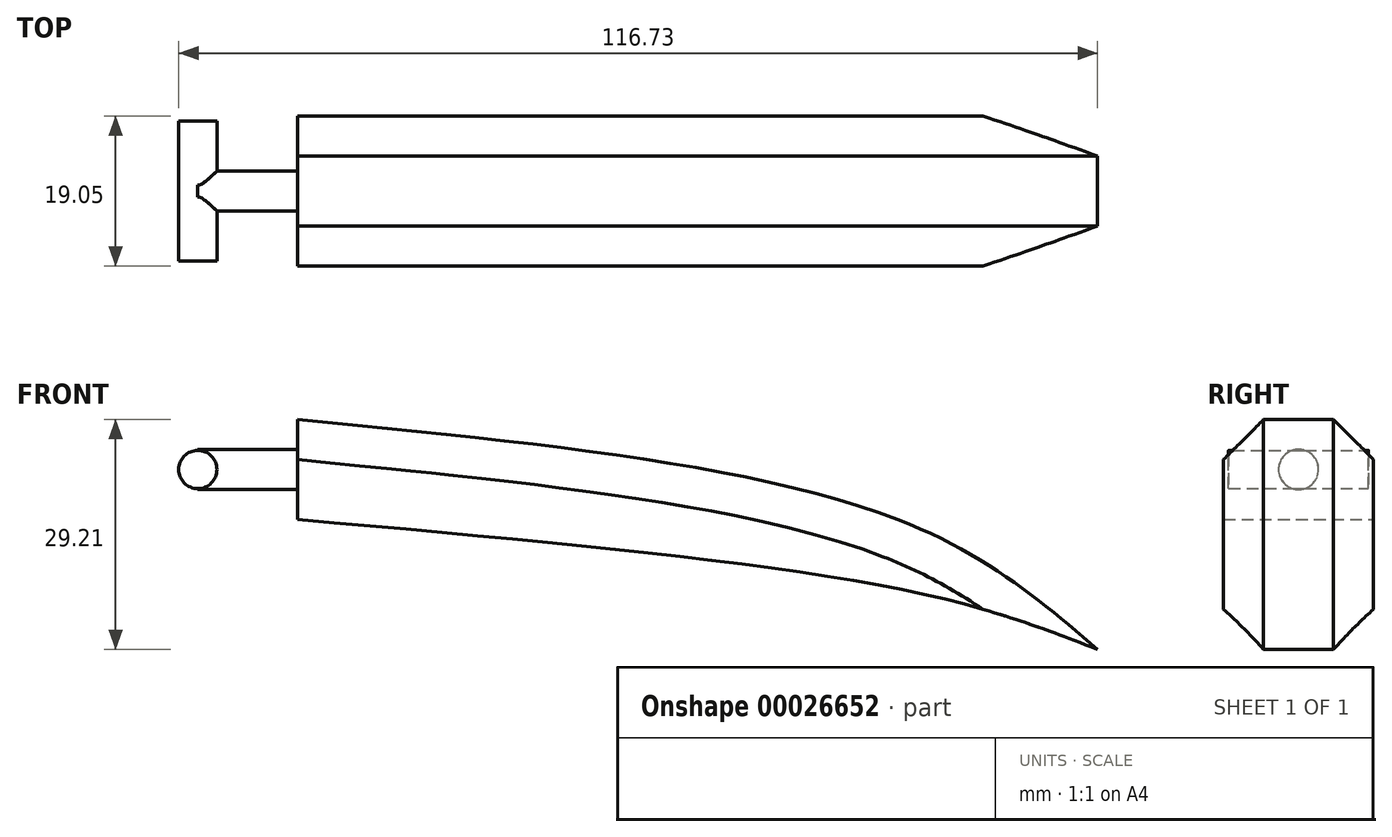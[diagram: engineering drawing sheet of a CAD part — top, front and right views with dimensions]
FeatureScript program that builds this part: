
annotation { "Feature Type Name" : "Feature", "Feature Type Description" : "" }
export const myFeature = defineFeature(function(context is Context, id is Id, definition is map)
    precondition{}
    {
        {
            var Q0;
            Q0=qCreatedBy(makeId("Front.planeOp"),FACE);
            var sketch = newSketch(context, id + "F0", { "sketchPlane" : qUnion([Q0])});
            skLineSegment(sketch, "E0.left", {"start": v(-50.09, 28.12) * mm, "end": v(-50.09, 40.82) * mm});
            skFitSpline(sketch, "E1", {"points": [v(-31.04, 40.82) * mm, v(26.11, 28.12) * mm, v(51.51, 11.61) * mm], "startDerivative": vector(109.54, -8.36) * mm, "endDerivative": vector(52.52, -44.36) * mm});
            skFitSpline(sketch, "E2", {"points": [v(-50.09, 28.12) * mm, v(28.13, 18.9) * mm, v(51.51, 11.61) * mm], "startDerivative": vector(139.98, -12.41) * mm, "endDerivative": vector(55.2, -21.46) * mm});
            skPoint(sketch, "E3.right.start.orphan", {"position": v(51.51, 31.93) * mm});
            skPoint(sketch, "E4.orphan", {"position": v(51.51, 40.82) * mm});
            skPoint(sketch, "E5.orphan", {"position": v(26.11, 40.82) * mm});
            skFitSpline(sketch, "E6", {"points": [v(-50.09, 40.82) * mm, v(26.11, 28.12) * mm, v(51.51, 11.61) * mm], "startDerivative": vector(141.74, -13.82) * mm, "endDerivative": vector(54.8, -47.15) * mm});
            skLineSegment(sketch, "E7.trimOffspring", {"start": v(51.51, 11.61) * mm, "end": v(51.51, 11.61) * mm});
            skSolve(sketch);
        }
        {
            var Q0;
            Q0 = qSketchRegion(id + "F0", true);
            extrude(context, id + "F1", {"entities" : qUnion([Q0]), "depth" : 19.05 * mm});
        }
        {
            var Q0;
            Q0=makeQuery(id+"F1.opExtrude","CAP_EDGE",EDGE,{"disambiguationData":[OSD([sQuery(id+"F0.wireOp",EDGE,"E6")])],"isStart":false});
            var Q1;
            Q1=makeQuery(id+"F1.opExtrude","CAP_EDGE",EDGE,{"disambiguationData":[OSD([sQuery(id+"F0.wireOp",EDGE,"E6")])],"isStart":true});
            var Q2;
            Q2=makeQuery(id+"F1.opExtrude","CAP_EDGE",EDGE,{"disambiguationData":[OSD([sQuery(id+"F0.wireOp",EDGE,"E1")])],"isStart":false});
            var Q3;
            Q3=makeQuery(id+"F1.opExtrude","CAP_EDGE",EDGE,{"disambiguationData":[OSD([sQuery(id+"F0.wireOp",EDGE,"E1")])],"isStart":true});
            chamfer(context, id + "F2", {"entities" : qUnion([Q0, Q1, Q2, Q3]), "width" : 5.08 * mm, "tangentPropagation" : true});
        }
        {
            var Q0;
            Q0=makeQuery(id+"F1.opExtrude","SWEPT_FACE",FACE,{"disambiguationData":[OSD([sQuery(id+"F0.wireOp",EDGE,"E0.left")])]});
            var sketch = newSketch(context, id + "F3", { "sketchPlane" : qUnion([Q0])});
            skCircle(sketch, "E8", {"center": v(9.53, 34.47) * mm, "radius": 2.54 * mm});
            skLineSegment(sketch, "E9", {"start": v(9.53, 28.12) * mm, "end": v(9.53, 40.82) * mm});
            skPoint(sketch, "E10", {"position": v(0, 35.72) * mm});
            skPoint(sketch, "E11", {"position": v(0, 28.12) * mm});
            skLineSegment(sketch, "E12", {"start": v(0, 35.72) * mm, "end": v(0, 28.12) * mm});
            skSolve(sketch);
        }
        {
            var Q0;
            Q0 = qSketchRegion(id + "F3", true);
            extrude(context, id + "F4", {"entities" : qUnion([Q0]), "operationType" : NewBodyOperationType.ADD, "depth" : 12.7 * mm});
        }
        {
            var Q0;
            Q0=makeQuery(id+"F4.opExtrude","CAP_FACE",FACE,{"disambiguationData":[OSD([sQuery(id+"F3.wireOp",EDGE,"E8")])],"isStart":false});
            var sketch = newSketch(context, id + "F5", { "sketchPlane" : qUnion([Q0])});
            skLineSegment(sketch, "E13.rect.bottom", {"start": v(0.64, 36.9) * mm, "end": v(18.42, 36.9) * mm});
            skLineSegment(sketch, "E13.rect.left", {"start": v(0.64, 36.9) * mm, "end": v(0.64, 34.47) * mm});
            skLineSegment(sketch, "E13.rect.right", {"start": v(18.42, 36.9) * mm, "end": v(18.42, 34.47) * mm});
            skPoint(sketch, "E13.rect.middle", {"position": v(9.53, 34.47) * mm});
            skLineSegment(sketch, "E14", {"start": v(0.64, 34.47) * mm, "end": v(18.42, 34.47) * mm});
            skPoint(sketch, "E13.rect.top.start.orphan", {"position": v(0.64, 32.04) * mm});
            skPoint(sketch, "E15.orphan", {"position": v(18.42, 32.04) * mm});
            skSolve(sketch);
        }
        {
            var Q0;
            Q0 = qSketchRegion(id + "F5", true);
            var Q1;
            Q1=sQuery(id+"F5.wireOp",EDGE,"E14");
            revolve(context, id + "F6", {"operationType" : NewBodyOperationType.ADD, "entities" : qUnion([Q0]), "axis" : qUnion([Q1]), "revolveType" : RevolveType.FULL});
        }
    });
